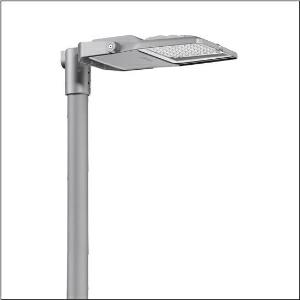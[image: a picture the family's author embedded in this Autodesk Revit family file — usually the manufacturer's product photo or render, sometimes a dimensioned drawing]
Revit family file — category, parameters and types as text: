
# Revit family: floodlight_fl_21_iq_mini___pl43_5xa7771c2a3a_69d2
name_source: partatom
category: Lighting Fixtures
units: mm (PartAtom-declared; Revit-internal decimal feet)

## family parameters
Cut with Voids When Loaded = No
Host = Face
Light Source = No
Part Type = Normal
Room Calculation Point = No
Round Connector Dimension = Use Diameter
Shared = No

## types (1)
- --- (1 x LED, 12520 lm, 87.2 W, 3000K)
    Apparent Load = 87 VA
    CIE Flux Codes = 27 78 99 100 100
    Color Rendering = 70
    Color Temperature = 3000K
    Default Elevation = 1800 mm
    Description = Floodlight FL 21 iQ mini, floodlight, primary light control with lens, of PMMA, primary optical cover: protective disc, of toughened safety glass, transparent, light distribution: PL43, light emission: direct distribution, installation type: surface-mounted, LED, High Power LED, rated luminous flux: 12.520lm, luminous efficacy: 144lm/W, light colour: 730, colour temperature: 3000K, control: Auto-Match, Temp-Guard, Lumen-Switch, Night-Set, Smart-Wire, Light-Fading, Desk-Remote (wireless, voltage-free reading and setting of iQ features in the workshop via application-optimized NFC function/RFID function), optimised constant luminous flux control (CLO 2.0), with terminal, 6-pole, mains connection: 220..240V, AC, 50/60Hz, start of lifetime: 87W, end of service life: 92W, reduction: 40W, luminaire housing, of diecast aluminium, powder-coated, Siteco® metallic grey (DB 702S), corrosivity category C5 mid according to DIN EN ISO 12944, sealing non-destructively replaceable, please order mast flange separately, mast bracket, of steel, galvanised, powder-coated, Siteco® metallic grey (DB 702S), protection rating (complete): IP66, insulation class (complete): insulation class II (safety insulation), certification: CE, ENEC, VDE, protection symbol: D, impact resistance: IK08, permissible operating ambient temperature: -40..+40°C, permissible operating ambient temperature for outdoor applications: -40..+50°C, standard: DIN EN 12944, LABS conformity tested according to VDMA 24364:2018-05, packaging unit: 1 piece

Light Distribution: PL43
    Height = 70 mm
    Lamp = 1 x LED
    Lamp Light Flux = 12520 lm
    Lamp Power = 87.2 W
    Lamp count = 1
    Length = 485 mm
    Luminous efficacy = 144 lm/W
    Manufacturer = Siteco
    ModVariant = No
    Model = 5XA7771C2A3A
    Number of Poles = 1
    OnlyDefault = Yes
    Power Factor = 1
    Product Name = Floodlight FL 21 iQ mini | PL43
    Product group = floodlight | pylon annexe
    ProductGroupID = 6200
    Protection Class = Protection class II
    Protection Degree = IP 66
    RLX_Detail_Level = 1
    RLX_Emergency_Light_Flux = 0 lm
    RLX_Emergency_Type = 0
    RLX_Emergency_Type_DB = No
    RlxData = <blob elided: 101201 chars, md5=9193fd17>
    Socket = socket
    Standby Power = 0 W
    System Light Flux = 12520 lm
    System Power = 87 W
    Type Comments = factory setting: luminous flux: 100 % | dim-lin: 254 | 456 mA
    Type Image = l_1007125.jpg
    URL = http://relux.com
    VarID = @adj_094801
    Voltage = 0 V
    Weight = 0.00 kg
    Width = 337 mm

## geometry (parser evidence)
native form markers: Blend x4, Sweep x15
no freeform markers — native parametric forms only
